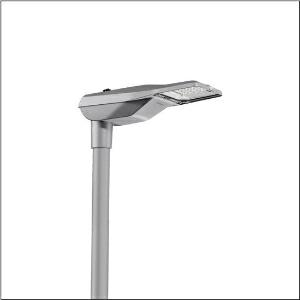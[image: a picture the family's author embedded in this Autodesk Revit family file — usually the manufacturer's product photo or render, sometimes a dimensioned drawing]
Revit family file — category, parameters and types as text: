
# Revit family: streetlight_sl_21_micro___st1_5a_5xe1p33s08db_10f0
name_source: partatom
category: Lighting Fixtures
units: mm (PartAtom-declared; Revit-internal decimal feet)

## family parameters
Cut with Voids When Loaded = No
Host = Face
Light Source = No
Part Type = Normal
Room Calculation Point = No
Round Connector Dimension = Use Diameter
Shared = No

## types (1)
- --- (1 x LED, 5020 lm, 39.1 W, 3000K)
    Apparent Load = 39 VA
    CIE Flux Codes = 22 53 95 100 100
    Color Rendering = 70
    Color Temperature = 3000K
    Default Elevation = 1800 mm
    Description = Streetlight SL 21 micro, mast luminaire, primary light control with lens, of PMMA, primary optical cover: cover, of toughened safety glass, transparent, light distribution: ST1.5a, light emission: direct distribution, primary light characteristic: asymmetric, installation type: side-entry, post-top, LED, High Power LED, rated luminous flux: 5.020lm, luminous efficacy: 128lm/W, light colour: 730, colour temperature: 3000K, control: flexible luminous flux parameterisation, time-dependent luminous flux control, constant luminous flux control, overheat protection, presetting dimming logarithmic, mains connection: 220..240V, AC, 50/60Hz, start of lifetime: 39W, end of service life: 41W, reduction: 18W, luminaire housing, of diecast aluminium, powder-coated, Siteco® metallic grey (DB 702S), corrosivity category C5 mid according to DIN EN ISO 12944, please order mast flange separately, inclination adjustable: 0°, 5°, 10°, 15°, sealing non-destructively replaceable, multi-level sealing system, length: 528mm, width: 235mm, height: 110mm, mast flange for spigot size: 42mm (side-entry): 5XC10008XM4, 60/48mm (side-entry/post-top): 5XC10108XM2, 76/60mm (side-entry/post-top): 5XC10108XM1, Smart Interface above, protection rating (complete): IP66, insulation class (complete): insulation class II (safety insulation), certification: CE, ENEC, ENEC+, VDE, impact resistance: IK09, permissible operating ambient temperature for outdoor applications: -40..+50°C, standard-compliant lighting for roads and squares, packaging unit: 1 piece

Light Distribution: ST1.5a
    Height = 110 mm
    Lamp = 1 x LED
    Lamp Light Flux = 5020 lm
    Lamp Power = 39.1 W
    Lamp count = 1
    Length = 528 mm
    Luminous efficacy = 128 lm/W
    Manufacturer = Siteco
    ModVariant = No
    Model = 5XE1P33S08DB
    Number of Poles = 1
    OnlyDefault = Yes
    Power Factor = 1
    Product Name = Streetlight SL 21 micro | ST1.5a
    Product group = mast luminaire | pylon top
    ProductGroupID = 6100
    Protection Class = Protection class II
    Protection Degree = IP 66
    RLX_Detail_Level = 1
    RLX_Emergency_Light_Flux = 0 lm
    RLX_Emergency_Type = 0
    RLX_Emergency_Type_DB = No
    RlxData = <blob elided: 102201 chars, md5=dc93ee48>
    Socket = socket
    Standby Power = 0 W
    System Light Flux = 5020 lm
    System Power = 39 W
    Type Comments = factory setting: luminous flux: 100 % | dim-lin: 254 | 765 mA
    Type Image = l_1277292.jpg
    URL = http://relux.com
    VarID = @adj_103905
    Voltage = 0 V
    Weight = 0.00 kg
    Width = 235 mm

## geometry (parser evidence)
native form markers: Blend x4, Sweep x9
no freeform markers — native parametric forms only
